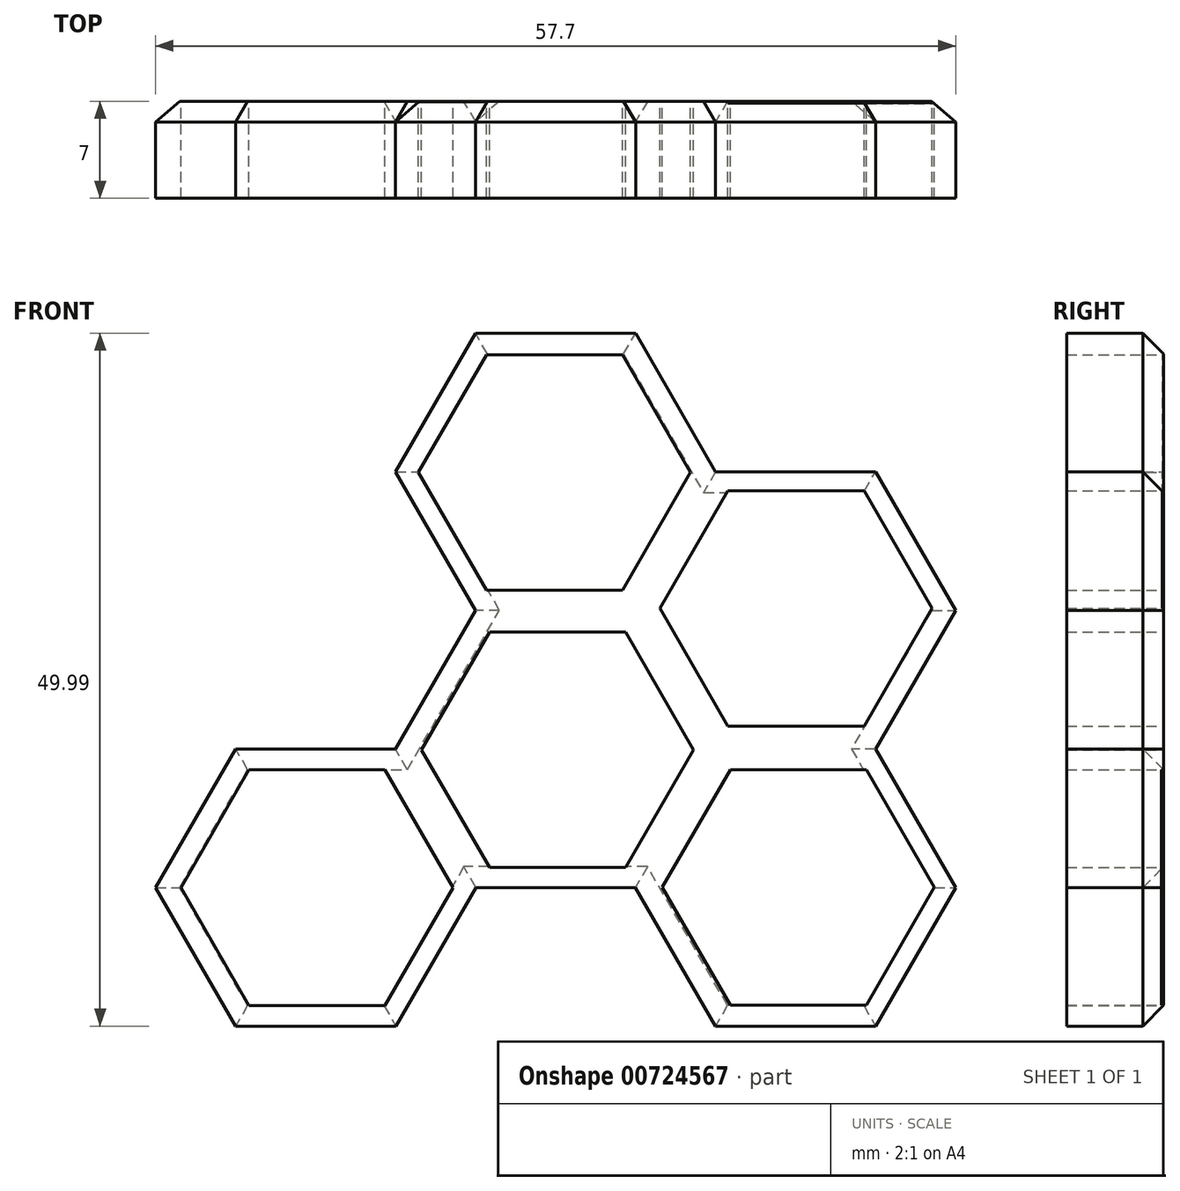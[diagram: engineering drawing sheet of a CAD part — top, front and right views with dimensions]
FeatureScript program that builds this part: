
annotation { "Feature Type Name" : "Feature", "Feature Type Description" : "" }
export const myFeature = defineFeature(function(context is Context, id is Id, definition is map)
    precondition{}
    {
        {
            var Q0;
            Q0=qCreatedBy(makeId("Front.planeOp"),FACE);
            var sketch = newSketch(context, id + "F0", { "sketchPlane" : qUnion([Q0])});
            skCircle(sketch, "E0.cCircle", {"center": v(-18.38, 0) * mm, "radius": 10 * mm, "construction": true});
            skLineSegment(sketch, "E0.0", {"start": v(-12.6, -10) * mm, "end": v(-24.15, -10) * mm});
            skLineSegment(sketch, "E0.1", {"start": v(-24.15, -10) * mm, "end": v(-29.93, 0) * mm});
            skLineSegment(sketch, "E0.2", {"start": v(-29.93, 0) * mm, "end": v(-24.15, 10) * mm});
            skLineSegment(sketch, "E0.3", {"start": v(-24.15, 10) * mm, "end": v(-12.6, 10) * mm});
            skLineSegment(sketch, "E0.4", {"start": v(-12.6, 10) * mm, "end": v(-6.83, 0) * mm});
            skLineSegment(sketch, "E0.5", {"start": v(-6.83, 0) * mm, "end": v(-12.6, -10) * mm});
            skPoint(sketch, "E0.0.midPoint", {"position": v(-18.38, -10) * mm});
            skSolve(sketch);
        }
        {
            var Q0;
            Q0=qCreatedBy(makeId("Front.planeOp"),FACE);
            var sketch = newSketch(context, id + "F1", { "sketchPlane" : qUnion([Q0])});
            skCircle(sketch, "E1.cCircle", {"center": v(-1.07, 10) * mm, "radius": 10 * mm, "construction": true});
            skLineSegment(sketch, "E1.0", {"start": v(4.7, 0) * mm, "end": v(-6.84, 0) * mm});
            skLineSegment(sketch, "E1.1", {"start": v(-6.84, 0) * mm, "end": v(-12.62, 10) * mm});
            skLineSegment(sketch, "E1.2", {"start": v(-12.62, 10) * mm, "end": v(-6.84, 20) * mm});
            skLineSegment(sketch, "E1.3", {"start": v(-6.84, 20) * mm, "end": v(4.7, 20) * mm});
            skLineSegment(sketch, "E1.4", {"start": v(4.7, 20) * mm, "end": v(10.48, 10) * mm});
            skLineSegment(sketch, "E1.5", {"start": v(10.48, 10) * mm, "end": v(4.7, 0) * mm});
            skPoint(sketch, "E1.0.midPoint", {"position": v(-1.07, 0) * mm});
            skSolve(sketch);
        }
        {
            var Q0;
            Q0=qCreatedBy(makeId("Front.planeOp"),FACE);
            var sketch = newSketch(context, id + "F2", { "sketchPlane" : qUnion([Q0])});
            skCircle(sketch, "E2.cCircle", {"center": v(-18.38, 20) * mm, "radius": 10 * mm, "construction": true});
            skLineSegment(sketch, "E2.0", {"start": v(-12.6, 10) * mm, "end": v(-24.15, 10) * mm});
            skLineSegment(sketch, "E2.1", {"start": v(-24.15, 10) * mm, "end": v(-29.92, 20) * mm});
            skLineSegment(sketch, "E2.2", {"start": v(-29.92, 20) * mm, "end": v(-24.15, 30) * mm});
            skLineSegment(sketch, "E2.3", {"start": v(-24.15, 30) * mm, "end": v(-12.6, 30) * mm});
            skLineSegment(sketch, "E2.4", {"start": v(-12.6, 30) * mm, "end": v(-6.83, 20) * mm});
            skLineSegment(sketch, "E2.5", {"start": v(-6.83, 20) * mm, "end": v(-12.6, 10) * mm});
            skPoint(sketch, "E2.0.midPoint", {"position": v(-18.38, 10) * mm});
            skSolve(sketch);
        }
        {
            var Q0;
            Q0=qCreatedBy(makeId("Front.planeOp"),FACE);
            var sketch = newSketch(context, id + "F3", { "sketchPlane" : qUnion([Q0])});
            skCircle(sketch, "E3.cCircle", {"center": v(-1.07, -10) * mm, "radius": 10 * mm, "construction": true});
            skLineSegment(sketch, "E3.0", {"start": v(4.7, -20) * mm, "end": v(-6.84, -20) * mm});
            skLineSegment(sketch, "E3.1", {"start": v(-6.84, -20) * mm, "end": v(-12.61, -10) * mm});
            skLineSegment(sketch, "E3.2", {"start": v(-12.61, -10) * mm, "end": v(-6.84, 0) * mm});
            skLineSegment(sketch, "E3.3", {"start": v(-6.84, 0) * mm, "end": v(4.7, 0) * mm});
            skLineSegment(sketch, "E3.4", {"start": v(4.7, 0) * mm, "end": v(10.48, -10) * mm});
            skLineSegment(sketch, "E3.5", {"start": v(10.48, -10) * mm, "end": v(4.7, -20) * mm});
            skPoint(sketch, "E3.0.midPoint", {"position": v(-1.07, -20) * mm});
            skSolve(sketch);
        }
        {
            var Q0;
            Q0=qCreatedBy(makeId("Front.planeOp"),FACE);
            var sketch = newSketch(context, id + "F4", { "sketchPlane" : qUnion([Q0])});
            skCircle(sketch, "E4.cCircle", {"center": v(-35.68, -10) * mm, "radius": 10 * mm, "construction": true});
            skLineSegment(sketch, "E4.0", {"start": v(-29.9, -20) * mm, "end": v(-41.45, -20) * mm});
            skLineSegment(sketch, "E4.1", {"start": v(-41.45, -20) * mm, "end": v(-47.22, -10) * mm});
            skLineSegment(sketch, "E4.2", {"start": v(-47.22, -10) * mm, "end": v(-41.45, 0) * mm});
            skLineSegment(sketch, "E4.3", {"start": v(-41.45, 0) * mm, "end": v(-29.9, 0) * mm});
            skLineSegment(sketch, "E4.4", {"start": v(-29.9, 0) * mm, "end": v(-24.13, -10) * mm});
            skLineSegment(sketch, "E4.5", {"start": v(-24.13, -10) * mm, "end": v(-29.9, -20) * mm});
            skPoint(sketch, "E4.0.midPoint", {"position": v(-35.68, -20) * mm});
            skSolve(sketch);
        }
        {
            var Q0;
            Q0 = qSketchRegion(id + "F2", true);
            extrude(context, id + "F5", {"entities" : qUnion([Q0]), "depth" : 7 * mm, "offsetDistance" : 25 * mm});
        }
        {
            var Q0;
            Q0=makeQuery(id+"F1.imprint","IMPRINT",FACE,{"disambiguationData":[TD([[makeQuery(id+"F1.imprint","IMPRINT",EDGE,{"derivedFrom":sQuery(id+"F1.wireOp",EDGE,"E1.0")}),-1.0]])]});
            extrude(context, id + "F6", {"entities" : qUnion([Q0]), "operationType" : NewBodyOperationType.ADD, "depth" : 7 * mm, "offsetDistance" : 25 * mm});
        }
        {
            var Q0;
            Q0 = qSketchRegion(id + "F0", true);
            extrude(context, id + "F7", {"entities" : qUnion([Q0]), "operationType" : NewBodyOperationType.ADD, "depth" : 7 * mm, "offsetDistance" : 25 * mm});
        }
        {
            var Q0;
            Q0 = qSketchRegion(id + "F4", true);
            extrude(context, id + "F8", {"entities" : qUnion([Q0]), "operationType" : NewBodyOperationType.ADD, "depth" : 7 * mm, "offsetDistance" : 25 * mm});
        }
        {
            var Q0;
            Q0 = qSketchRegion(id + "F3", true);
            extrude(context, id + "F9", {"entities" : qUnion([Q0]), "operationType" : NewBodyOperationType.ADD, "depth" : 7 * mm, "offsetDistance" : 25 * mm});
        }
        {
            var Q0;
            Q0=qCreatedBy(makeId("Front.planeOp"),FACE);
            var sketch = newSketch(context, id + "F10", { "sketchPlane" : qUnion([Q0])});
            skCircle(sketch, "E5.cCircle", {"center": v(-1.03, 10.14) * mm, "radius": 8.5 * mm, "construction": true});
            skLineSegment(sketch, "E5.0", {"start": v(-5.94, 18.64) * mm, "end": v(3.87, 18.64) * mm});
            skLineSegment(sketch, "E5.1", {"start": v(3.87, 18.64) * mm, "end": v(8.78, 10.14) * mm});
            skLineSegment(sketch, "E5.2", {"start": v(8.78, 10.14) * mm, "end": v(3.87, 1.64) * mm});
            skLineSegment(sketch, "E5.3", {"start": v(3.87, 1.64) * mm, "end": v(-5.94, 1.64) * mm});
            skLineSegment(sketch, "E5.4", {"start": v(-5.94, 1.64) * mm, "end": v(-10.85, 10.14) * mm});
            skLineSegment(sketch, "E5.5", {"start": v(-10.85, 10.14) * mm, "end": v(-5.94, 18.64) * mm});
            skPoint(sketch, "E5.0.midPoint", {"position": v(-1.03, 18.64) * mm});
            skCircle(sketch, "E6.cCircle", {"center": v(-18.23, -0.06) * mm, "radius": 8.5 * mm, "construction": true});
            skLineSegment(sketch, "E6.0", {"start": v(-23.14, 8.44) * mm, "end": v(-13.33, 8.44) * mm});
            skLineSegment(sketch, "E6.1", {"start": v(-13.33, 8.44) * mm, "end": v(-8.42, -0.06) * mm});
            skLineSegment(sketch, "E6.2", {"start": v(-8.42, -0.06) * mm, "end": v(-13.33, -8.56) * mm});
            skLineSegment(sketch, "E6.3", {"start": v(-13.33, -8.56) * mm, "end": v(-23.14, -8.56) * mm});
            skLineSegment(sketch, "E6.4", {"start": v(-23.14, -8.56) * mm, "end": v(-28.05, -0.06) * mm});
            skLineSegment(sketch, "E6.5", {"start": v(-28.05, -0.06) * mm, "end": v(-23.14, 8.44) * mm});
            skPoint(sketch, "E6.0.midPoint", {"position": v(-18.23, 8.44) * mm});
            skCircle(sketch, "E7.cCircle", {"center": v(-0.87, -9.99) * mm, "radius": 8.5 * mm, "construction": true});
            skLineSegment(sketch, "E7.0", {"start": v(-5.78, -1.49) * mm, "end": v(4.04, -1.49) * mm});
            skLineSegment(sketch, "E7.1", {"start": v(4.04, -1.49) * mm, "end": v(8.94, -9.99) * mm});
            skLineSegment(sketch, "E7.2", {"start": v(8.94, -9.99) * mm, "end": v(4.04, -18.49) * mm});
            skLineSegment(sketch, "E7.3", {"start": v(4.04, -18.49) * mm, "end": v(-5.78, -18.49) * mm});
            skLineSegment(sketch, "E7.4", {"start": v(-5.78, -18.49) * mm, "end": v(-10.69, -9.99) * mm});
            skLineSegment(sketch, "E7.5", {"start": v(-10.69, -9.99) * mm, "end": v(-5.78, -1.49) * mm});
            skPoint(sketch, "E7.0.midPoint", {"position": v(-0.87, -1.49) * mm});
            skCircle(sketch, "E8.cCircle", {"center": v(-35.58, -10.02) * mm, "radius": 8.5 * mm, "construction": true});
            skLineSegment(sketch, "E8.0", {"start": v(-40.49, -1.52) * mm, "end": v(-30.67, -1.52) * mm});
            skLineSegment(sketch, "E8.1", {"start": v(-30.67, -1.52) * mm, "end": v(-25.77, -10.02) * mm});
            skLineSegment(sketch, "E8.2", {"start": v(-25.77, -10.02) * mm, "end": v(-30.67, -18.52) * mm});
            skLineSegment(sketch, "E8.3", {"start": v(-30.67, -18.52) * mm, "end": v(-40.49, -18.52) * mm});
            skLineSegment(sketch, "E8.4", {"start": v(-40.49, -18.52) * mm, "end": v(-45.4, -10.02) * mm});
            skLineSegment(sketch, "E8.5", {"start": v(-45.4, -10.02) * mm, "end": v(-40.49, -1.52) * mm});
            skPoint(sketch, "E8.0.midPoint", {"position": v(-35.58, -1.52) * mm});
            skCircle(sketch, "E9.cCircle", {"center": v(-18.46, 19.95) * mm, "radius": 8.5 * mm, "construction": true});
            skLineSegment(sketch, "E9.0", {"start": v(-23.37, 28.45) * mm, "end": v(-13.55, 28.45) * mm});
            skLineSegment(sketch, "E9.1", {"start": v(-13.55, 28.45) * mm, "end": v(-8.65, 19.95) * mm});
            skLineSegment(sketch, "E9.2", {"start": v(-8.65, 19.95) * mm, "end": v(-13.55, 11.45) * mm});
            skLineSegment(sketch, "E9.3", {"start": v(-13.55, 11.45) * mm, "end": v(-23.37, 11.45) * mm});
            skLineSegment(sketch, "E9.4", {"start": v(-23.37, 11.45) * mm, "end": v(-28.28, 19.95) * mm});
            skLineSegment(sketch, "E9.5", {"start": v(-28.28, 19.95) * mm, "end": v(-23.37, 28.45) * mm});
            skPoint(sketch, "E9.0.midPoint", {"position": v(-18.46, 28.45) * mm});
            skSolve(sketch);
        }
        {
            var Q0;
            Q0=makeQuery(id+"F5.opExtrude","CAP_EDGE",EDGE,{"disambiguationData":[OSD([sQuery(id+"F2.wireOp",EDGE,"E2.4")])],"isStart":true});
            var Q1;
            Q1=makeQuery(id+"F5.opExtrude","CAP_EDGE",EDGE,{"disambiguationData":[OSD([sQuery(id+"F2.wireOp",EDGE,"E2.3")])],"isStart":true});
            var Q2;
            Q2=makeQuery(id+"F5.opExtrude","CAP_EDGE",EDGE,{"disambiguationData":[OSD([sQuery(id+"F2.wireOp",EDGE,"E2.2")])],"isStart":true});
            var Q3;
            Q3=makeQuery(id+"F5.opExtrude","CAP_EDGE",EDGE,{"disambiguationData":[OSD([sQuery(id+"F2.wireOp",EDGE,"E2.1")])],"isStart":true});
            var Q4;
            Q4=makeQuery(id+"F7.opExtrude","CAP_EDGE",EDGE,{"disambiguationData":[OSD([sQuery(id+"F0.wireOp",EDGE,"E0.2")])],"isStart":true});
            var Q5;
            Q5=makeQuery(id+"F8.opExtrude","CAP_EDGE",EDGE,{"disambiguationData":[OSD([sQuery(id+"F4.wireOp",EDGE,"E4.3")])],"isStart":true});
            var Q6;
            Q6=makeQuery(id+"F8.opExtrude","CAP_EDGE",EDGE,{"disambiguationData":[OSD([sQuery(id+"F4.wireOp",EDGE,"E4.2")])],"isStart":true});
            var Q7;
            Q7=makeQuery(id+"F8.opExtrude","CAP_EDGE",EDGE,{"disambiguationData":[OSD([sQuery(id+"F4.wireOp",EDGE,"E4.1")])],"isStart":true});
            var Q8;
            Q8=makeQuery(id+"F8.opExtrude","CAP_EDGE",EDGE,{"disambiguationData":[OSD([sQuery(id+"F4.wireOp",EDGE,"E4.0")])],"isStart":true});
            var Q9;
            Q9=makeQuery(id+"F8.opExtrude","CAP_EDGE",EDGE,{"disambiguationData":[OSD([sQuery(id+"F4.wireOp",EDGE,"E4.5")])],"isStart":true});
            var Q10;
            Q10=makeQuery(id+"F7.opExtrude","CAP_EDGE",EDGE,{"disambiguationData":[OSD([sQuery(id+"F0.wireOp",EDGE,"E0.0")])],"isStart":true});
            var Q11;
            Q11=makeQuery(id+"F9.opExtrude","CAP_EDGE",EDGE,{"disambiguationData":[OSD([sQuery(id+"F3.wireOp",EDGE,"E3.1")])],"isStart":true});
            var Q12;
            Q12=makeQuery(id+"F9.opExtrude","CAP_EDGE",EDGE,{"disambiguationData":[OSD([sQuery(id+"F3.wireOp",EDGE,"E3.0")])],"isStart":true});
            var Q13;
            Q13=makeQuery(id+"F9.opExtrude","CAP_EDGE",EDGE,{"disambiguationData":[OSD([sQuery(id+"F3.wireOp",EDGE,"E3.5")])],"isStart":true});
            var Q14;
            Q14=makeQuery(id+"F9.opExtrude","CAP_EDGE",EDGE,{"disambiguationData":[OSD([sQuery(id+"F3.wireOp",EDGE,"E3.4")])],"isStart":true});
            var Q15;
            Q15=makeQuery(id+"F6.opExtrude","CAP_EDGE",EDGE,{"disambiguationData":[OSD([sQuery(id+"F1.wireOp",EDGE,"E1.5")])],"isStart":true});
            var Q16;
            Q16=makeQuery(id+"F6.opExtrude","CAP_EDGE",EDGE,{"disambiguationData":[OSD([sQuery(id+"F1.wireOp",EDGE,"E1.4")])],"isStart":true});
            var Q17;
            Q17=makeQuery(id+"F6.opExtrude","CAP_EDGE",EDGE,{"disambiguationData":[OSD([sQuery(id+"F1.wireOp",EDGE,"E1.3")])],"isStart":true});
            chamfer(context, id + "F11", {"entities" : qUnion([Q0, Q1, Q2, Q3, Q4, Q5, Q6, Q7, Q8, Q9, Q10, Q11, Q12, Q13, Q14, Q15, Q16, Q17]), "width" : 1.5 * mm, "tangentPropagation" : true});
        }
        {
            var Q0;
            Q0=makeQuery(id+"F10.imprint","IMPRINT",FACE,{"disambiguationData":[TD([[makeQuery(id+"F10.imprint","IMPRINT",EDGE,{"derivedFrom":sQuery(id+"F10.wireOp",EDGE,"E5.0")}),-1.0]])]});
            var Q1;
            Q1=makeQuery(id+"F10.imprint","IMPRINT",FACE,{"disambiguationData":[TD([[makeQuery(id+"F10.imprint","IMPRINT",EDGE,{"derivedFrom":sQuery(id+"F10.wireOp",EDGE,"E9.0")}),-1.0]])]});
            var Q2;
            Q2=makeQuery(id+"F10.imprint","IMPRINT",FACE,{"disambiguationData":[TD([[makeQuery(id+"F10.imprint","IMPRINT",EDGE,{"derivedFrom":sQuery(id+"F10.wireOp",EDGE,"E6.0")}),-1.0]])]});
            var Q3;
            Q3=makeQuery(id+"F10.imprint","IMPRINT",FACE,{"disambiguationData":[TD([[makeQuery(id+"F10.imprint","IMPRINT",EDGE,{"derivedFrom":sQuery(id+"F10.wireOp",EDGE,"E7.0")}),-1.0]])]});
            var Q4;
            Q4=makeQuery(id+"F10.imprint","IMPRINT",FACE,{"disambiguationData":[TD([[makeQuery(id+"F10.imprint","IMPRINT",EDGE,{"derivedFrom":sQuery(id+"F10.wireOp",EDGE,"E8.0")}),-1.0]])]});
            extrude(context, id + "F12", {"entities" : qUnion([Q0, Q1, Q2, Q3, Q4]), "operationType" : NewBodyOperationType.REMOVE, "depth" : 7 * mm, "offsetDistance" : 25 * mm});
        }
    });
